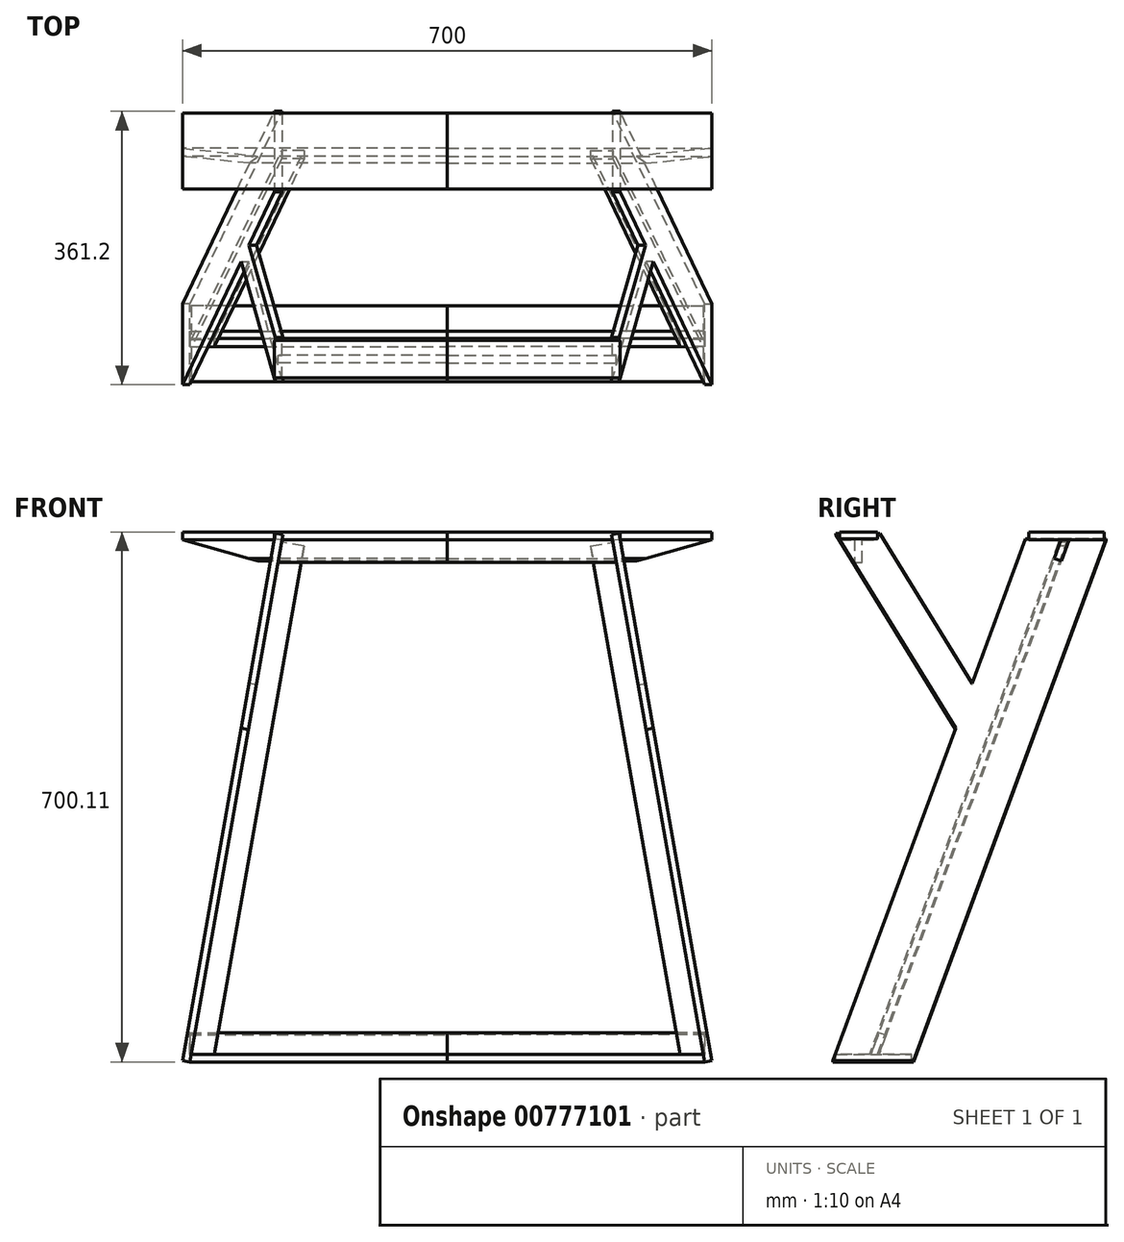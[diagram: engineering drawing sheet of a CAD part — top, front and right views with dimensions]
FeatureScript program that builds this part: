
annotation { "Feature Type Name" : "Feature", "Feature Type Description" : "" }
export const myFeature = defineFeature(function(context is Context, id is Id, definition is map)
    precondition{}
    {
        {
            var Q0;
            Q0=qCreatedBy(makeId("Right.planeOp"),FACE);
            cPlane(context, id + "F0", {"entities" : qUnion([Q0]), "cplaneType" : CPlaneType.OFFSET, "offset" : 350 * mm, "width" : 150 * mm, "height" : 150 * mm});
        }
        {
            var Q0;
            Q0=qCreatedBy(makeId("Right.planeOp"),FACE);
            cPlane(context, id + "F1", {"entities" : qUnion([Q0]), "cplaneType" : CPlaneType.OFFSET, "offset" : 0 * mm, "oppositeDirection" : true, "width" : 150 * mm, "height" : 150 * mm});
        }
        {
            var Q0;
            Q0=qCreatedBy(makeId("Top.planeOp"),FACE);
            var sketch = newSketch(context, id + "F2", { "sketchPlane" : qUnion([Q0])});
            skLineSegment(sketch, "E0", {"start": v(0, 0) * mm, "end": v(0, 250.53) * mm, "construction": true});
            skSolve(sketch);
        }
        {
            var Q0;
            Q0=sQuery(id+"F2.wireOp",EDGE,"E0");
            var Q1;
            Q1=qCreatedBy(makeId("Top.planeOp"),FACE);
            cPlane(context, id + "F3", {"entities" : qUnion([Q0, Q1]), "cplaneType" : CPlaneType.LINE_ANGLE, "offset" : 25 * mm, "angle" : 80 * degree, "oppositeDirection" : true, "width" : 150 * mm, "height" : 150 * mm});
        }
        {
            var Q0;
            Q0=qCreatedBy(id+"F3.planeOp",FACE);
            var sketch = newSketch(context, id + "F4", { "sketchPlane" : qUnion([Q0])});
            skLineSegment(sketch, "E1", {"start": v(0, 0) * mm, "end": v(254.78, 700) * mm});
            skLineSegment(sketch, "E2", {"start": v(254.78, 700) * mm, "end": v(148.36, 700) * mm});
            skLineSegment(sketch, "E3", {"start": v(148.36, 700) * mm, "end": v(-106.42, 0) * mm});
            skLineSegment(sketch, "E4", {"start": v(-106.42, 0) * mm, "end": v(0, 0) * mm});
            skSolve(sketch);
        }
        {
            var Q0;
            Q0 = qSketchRegion(id + "F4", true);
            extrude(context, id + "F5", {"entities" : qUnion([Q0]), "depth" : 10 * mm, "offsetDistance" : 25 * mm});
        }
        {
            var Q0;
            Q0=qCreatedBy(makeId("Right.planeOp"),FACE);
            var Q1;
            Q1=makeQuery(id+"F5.opExtrude","CAP_EDGE",EDGE,{"disambiguationData":[OSD([sQuery(id+"F4.wireOp",EDGE,"E2")])],"isStart":true});
            cPlane(context, id + "F6", {"entities" : qUnion([Q0, Q1]), "cplaneType" : CPlaneType.LINE_ANGLE, "offset" : 25 * mm, "angle" : 0 * degree, "width" : 150 * mm, "height" : 150 * mm});
        }
        {
            var Q0;
            Q0=qCreatedBy(makeId("Right.planeOp"),FACE);
            var Q1;
            Q1=makeQuery(id+"F5.opExtrude","CAP_EDGE",EDGE,{"disambiguationData":[OSD([sQuery(id+"F4.wireOp",EDGE,"E4")])],"isStart":false});
            cPlane(context, id + "F7", {"entities" : qUnion([Q0, Q1]), "cplaneType" : CPlaneType.LINE_ANGLE, "offset" : 25 * mm, "angle" : 0 * degree, "width" : 150 * mm, "height" : 150 * mm});
        }
        {
            var Q0;
            Q0=qCreatedBy(id+"F7.planeOp",FACE);
            var sketch = newSketch(context, id + "F8", { "sketchPlane" : qUnion([Q0])});
            skLineSegment(sketch, "E5.bottom", {"start": v(102.5, 8.26) * mm, "end": v(2.5, 8.26) * mm});
            skLineSegment(sketch, "E5.top", {"start": v(102.5, -1.74) * mm, "end": v(2.5, -1.74) * mm});
            skLineSegment(sketch, "E5.left", {"start": v(102.5, 8.26) * mm, "end": v(102.5, -1.74) * mm});
            skLineSegment(sketch, "E5.right", {"start": v(2.5, 8.26) * mm, "end": v(2.5, -1.74) * mm});
            skSolve(sketch);
        }
        {
            var Q0;
            Q0 = qSketchRegion(id + "F8", true);
            var Q1;
            Q1=qCreatedBy(id+"F0.planeOp",FACE);
            extrude(context, id + "F9", {"entities" : qUnion([Q0]), "operationType" : NewBodyOperationType.ADD, "endBound" : BoundingType.UP_TO_SURFACE, "oppositeDirection" : true, "depth" : 25 * mm, "endBoundEntityFace" : qUnion([Q1]), "offsetDistance" : 25 * mm});
        }
        {
            var Q0;
            Q0=qCreatedBy(id+"F1.planeOp",FACE);
            var sketch = newSketch(context, id + "F10", { "sketchPlane" : qUnion([Q0])});
            skLineSegment(sketch, "E6.bottom", {"start": v(152.28, 688.37) * mm, "end": v(252.28, 688.37) * mm});
            skLineSegment(sketch, "E6.top", {"start": v(152.28, 698.37) * mm, "end": v(252.28, 698.37) * mm});
            skLineSegment(sketch, "E6.left", {"start": v(152.28, 688.37) * mm, "end": v(152.28, 698.37) * mm});
            skLineSegment(sketch, "E6.right", {"start": v(252.28, 688.37) * mm, "end": v(252.28, 698.37) * mm});
            skSolve(sketch);
        }
        {
            var Q0;
            Q0 = qSketchRegion(id + "F10", true);
            var Q1;
            Q1=qCreatedBy(id+"F0.planeOp",FACE);
            extrude(context, id + "F11", {"entities" : qUnion([Q0]), "endBound" : BoundingType.UP_TO_SURFACE, "depth" : 25 * mm, "endBoundEntityFace" : qUnion([Q1]), "offsetDistance" : 25 * mm});
        }
        {
            var Q0;
            Q0=makeQuery(id+"F5.opExtrude","CAP_FACE",FACE,{"disambiguationData":[OSD([sQuery(id+"F4.wireOp",EDGE,"E1"),sQuery(id+"F4.wireOp",EDGE,"E2"),sQuery(id+"F4.wireOp",EDGE,"E3"),sQuery(id+"F4.wireOp",EDGE,"E4")])],"isStart":false});
            var sketch = newSketch(context, id + "F12", { "sketchPlane" : qUnion([Q0])});
            skLineSegment(sketch, "E7", {"start": v(192.15, 697.67) * mm, "end": v(-58.14, 10) * mm});
            skLineSegment(sketch, "E8", {"start": v(-58.14, 10) * mm, "end": v(-47.5, 10) * mm});
            skLineSegment(sketch, "E9", {"start": v(-47.5, 10) * mm, "end": v(202.79, 697.67) * mm});
            skLineSegment(sketch, "E10", {"start": v(202.79, 697.67) * mm, "end": v(192.15, 697.67) * mm});
            skSolve(sketch);
        }
        {
            var Q0;
            Q0 = qSketchRegion(id + "F12", true);
            extrude(context, id + "F13", {"entities" : qUnion([Q0]), "depth" : 30 * mm, "offsetDistance" : 25 * mm});
        }
        {
            var Q0;
            Q0=qCreatedBy(id+"F1.planeOp",FACE);
            var sketch = newSketch(context, id + "F14", { "sketchPlane" : qUnion([Q0])});
            skLineSegment(sketch, "E11", {"start": v(195.2, 688.37) * mm, "end": v(186.07, 663.69) * mm});
            skLineSegment(sketch, "E12", {"start": v(195.44, 660.23) * mm, "end": v(205.84, 688.37) * mm});
            skLineSegment(sketch, "E13", {"start": v(205.84, 688.37) * mm, "end": v(195.2, 688.37) * mm});
            skLineSegment(sketch, "E14", {"start": v(195.44, 660.23) * mm, "end": v(186.07, 663.69) * mm});
            skSolve(sketch);
        }
        {
            var Q0;
            Q0 = qSketchRegion(id + "F14", true);
            var Q1;
            Q1=qCreatedBy(id+"F0.planeOp",FACE);
            extrude(context, id + "F15", {"entities" : qUnion([Q0]), "endBound" : BoundingType.UP_TO_SURFACE, "depth" : 408 * mm, "endBoundEntityFace" : qUnion([Q1]), "offsetDistance" : 25 * mm});
        }
        {
            var Q0;
            Q0=qCreatedBy(id+"F0.planeOp",FACE);
            var sketch = newSketch(context, id + "F16", { "sketchPlane" : qUnion([Q0])});
            skLineSegment(sketch, "E15", {"start": v(-45.52, 8.26) * mm, "end": v(-56.16, 8.26) * mm});
            skLineSegment(sketch, "E16", {"start": v(-56.16, 8.26) * mm, "end": v(-45.7, 36.6) * mm});
            skLineSegment(sketch, "E17", {"start": v(-45.7, 36.6) * mm, "end": v(-35.93, 34.21) * mm});
            skLineSegment(sketch, "E18", {"start": v(-35.93, 34.21) * mm, "end": v(-45.52, 8.26) * mm});
            skSolve(sketch);
        }
        {
            var Q0;
            Q0 = qSketchRegion(id + "F16", true);
            var Q1;
            Q1=qCreatedBy(id+"F7.planeOp",FACE);
            extrude(context, id + "F17", {"entities" : qUnion([Q0]), "endBound" : BoundingType.UP_TO_SURFACE, "oppositeDirection" : true, "depth" : 216 * mm, "endBoundEntityFace" : qUnion([Q1]), "offsetDistance" : 25 * mm});
        }
        {
            var Q0;
            Q0=qCreatedBy(id+"F6.planeOp",FACE);
            var sketch = newSketch(context, id + "F18", { "sketchPlane" : qUnion([Q0])});
            skLineSegment(sketch, "E19", {"start": v(126.14, 698.37) * mm, "end": v(-231.07, 698.37) * mm, "construction": true});
            skLineSegment(sketch, "E20", {"start": v(47.72, 698.37) * mm, "end": v(97.72, 698.37) * mm});
            skLineSegment(sketch, "E21", {"start": v(97.72, 698.37) * mm, "end": v(97.72, 688.37) * mm});
            skLineSegment(sketch, "E22", {"start": v(97.72, 688.37) * mm, "end": v(77.72, 688.37) * mm});
            skLineSegment(sketch, "E23", {"start": v(77.72, 688.37) * mm, "end": v(77.72, 658.37) * mm});
            skLineSegment(sketch, "E24", {"start": v(77.72, 658.37) * mm, "end": v(67.72, 658.37) * mm});
            skLineSegment(sketch, "E25", {"start": v(67.72, 658.37) * mm, "end": v(67.72, 688.37) * mm});
            skLineSegment(sketch, "E26", {"start": v(67.72, 688.37) * mm, "end": v(47.72, 688.37) * mm});
            skLineSegment(sketch, "E27", {"start": v(47.72, 698.37) * mm, "end": v(47.72, 688.37) * mm});
            skSolve(sketch);
        }
        {
            var Q0;
            Q0 = qSketchRegion(id + "F18", true);
            var Q1;
            Q1=qCreatedBy(id+"F0.planeOp",FACE);
            extrude(context, id + "F19", {"entities" : qUnion([Q0]), "endBound" : BoundingType.UP_TO_SURFACE, "oppositeDirection" : true, "depth" : 25 * mm, "endBoundEntityFace" : qUnion([Q1]), "offsetDistance" : 25 * mm});
        }
        {
            var Q0;
            Q0=qCreatedBy(id+"F3.planeOp",FACE);
            var sketch = newSketch(context, id + "F20", { "sketchPlane" : qUnion([Q0])});
            skLineSegment(sketch, "E28", {"start": v(-102.9, 707.55) * mm, "end": v(83.8, 400) * mm});
            skLineSegment(sketch, "E29", {"start": v(83.8, 400) * mm, "end": v(105.73, 460.24) * mm});
            skLineSegment(sketch, "E30", {"start": v(105.73, 460.24) * mm, "end": v(-44.4, 707.55) * mm});
            skLineSegment(sketch, "E31", {"start": v(-44.4, 707.55) * mm, "end": v(-102.9, 707.55) * mm});
            skSolve(sketch);
        }
        {
            var Q0;
            Q0 = qSketchRegion(id + "F20", true);
            extrude(context, id + "F21", {"entities" : qUnion([Q0]), "operationType" : NewBodyOperationType.ADD, "depth" : 10 * mm, "offsetDistance" : 25 * mm});
        }
        {
            var Q0;
            Q0=makeQuery(id+"F11.opExtrude","SWEPT_FACE",FACE,{"disambiguationData":[OSD([sQuery(id+"F10.wireOp",EDGE,"E6.left")])]});
            var sketch = newSketch(context, id + "F22", { "sketchPlane" : qUnion([Q0])});
            skLineSegment(sketch, "E32", {"start": v(0, 688.37) * mm, "end": v(100, 660.23) * mm});
            skLineSegment(sketch, "E33", {"start": v(100, 660.23) * mm, "end": v(0, 660.23) * mm});
            skLineSegment(sketch, "E34", {"start": v(0, 660.23) * mm, "end": v(0, 688.37) * mm});
            skSolve(sketch);
        }
        {
            var Q0;
            Q0 = qSketchRegion(id + "F22", true);
            extrude(context, id + "F23", {"entities" : qUnion([Q0]), "operationType" : NewBodyOperationType.REMOVE, "endBound" : BoundingType.THROUGH_ALL, "oppositeDirection" : true, "depth" : 25 * mm, "offsetDistance" : 25 * mm});
        }
        {
            var Q0;
            Q0=makeQuery(id+"F11.opExtrude","SWEPT_BODY",BODY,{"disambiguationData":[OSD([sQuery(id+"F10.wireOp",EDGE,"E6.bottom"),sQuery(id+"F10.wireOp",EDGE,"E6.top"),sQuery(id+"F10.wireOp",EDGE,"E6.left"),sQuery(id+"F10.wireOp",EDGE,"E6.right")])]});
            var Q1;
            Q1=makeQuery(id+"F5.opExtrude","SWEPT_BODY",BODY,{"disambiguationData":[OSD([sQuery(id+"F4.wireOp",EDGE,"E1"),sQuery(id+"F4.wireOp",EDGE,"E2"),sQuery(id+"F4.wireOp",EDGE,"E3"),sQuery(id+"F4.wireOp",EDGE,"E4")])]});
            var Q2;
            Q2=makeQuery(id+"F13.opExtrude","SWEPT_BODY",BODY,{"disambiguationData":[OSD([sQuery(id+"F12.wireOp",EDGE,"E7"),sQuery(id+"F12.wireOp",EDGE,"E8"),sQuery(id+"F12.wireOp",EDGE,"E9"),sQuery(id+"F12.wireOp",EDGE,"E10")])]});
            var Q3;
            Q3=makeQuery(id+"F19.opExtrude","SWEPT_BODY",BODY,{"disambiguationData":[OSD([sQuery(id+"F18.wireOp",EDGE,"E20"),sQuery(id+"F18.wireOp",EDGE,"E21"),sQuery(id+"F18.wireOp",EDGE,"E22"),sQuery(id+"F18.wireOp",EDGE,"E23"),sQuery(id+"F18.wireOp",EDGE,"E24"),sQuery(id+"F18.wireOp",EDGE,"E25"),sQuery(id+"F18.wireOp",EDGE,"E26"),sQuery(id+"F18.wireOp",EDGE,"E27")])]});
            var Q4;
            Q4=makeQuery(id+"F15.opExtrude","SWEPT_BODY",BODY,{"disambiguationData":[OSD([sQuery(id+"F14.wireOp",EDGE,"E11"),sQuery(id+"F14.wireOp",EDGE,"E12"),sQuery(id+"F14.wireOp",EDGE,"E13"),sQuery(id+"F14.wireOp",EDGE,"E14")])]});
            var Q5;
            Q5=makeQuery(id+"F17.opExtrude","SWEPT_BODY",BODY,{"disambiguationData":[OSD([sQuery(id+"F16.wireOp",EDGE,"E15"),sQuery(id+"F16.wireOp",EDGE,"E16"),sQuery(id+"F16.wireOp",EDGE,"E17"),sQuery(id+"F16.wireOp",EDGE,"E18")])]});
            var Q6;
            Q6=qCreatedBy(id+"F0.planeOp",FACE);
            mirror(context, id + "F24", {"entities" : qUnion([Q0, Q1, Q2, Q3, Q4, Q5]), "mirrorPlane" : qUnion([Q6])});
        }
    });
